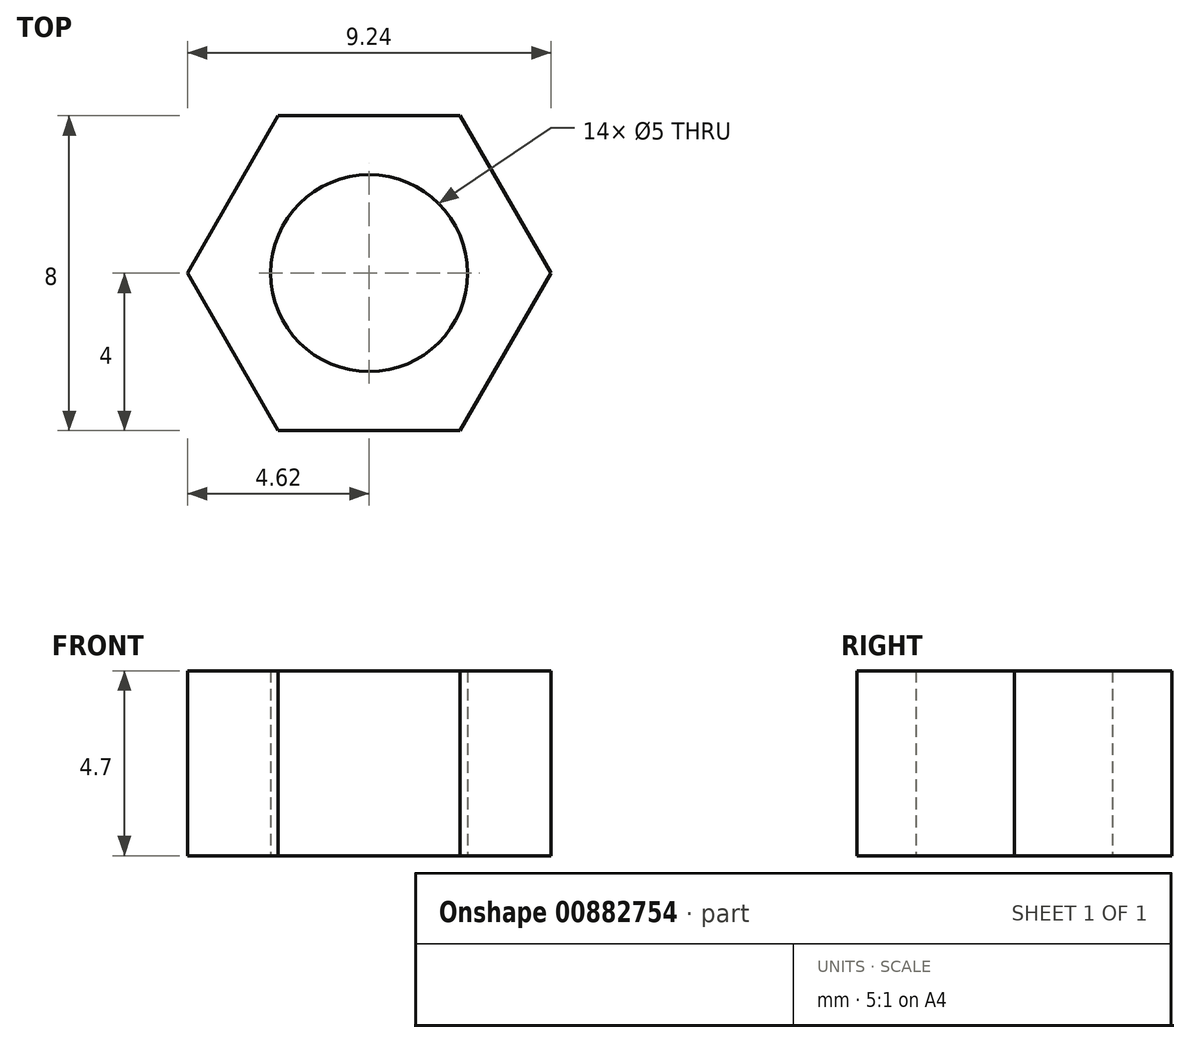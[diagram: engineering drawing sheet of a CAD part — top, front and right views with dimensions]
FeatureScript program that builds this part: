
annotation { "Feature Type Name" : "Feature", "Feature Type Description" : "" }
export const myFeature = defineFeature(function(context is Context, id is Id, definition is map)
    precondition{}
    {
        {
            var Q0;
            Q0=qCreatedBy(makeId("Top.planeOp"),FACE);
            var sketch = newSketch(context, id + "F0", { "sketchPlane" : qUnion([Q0])});
            skCircle(sketch, "E0", {"center": v(0, 0) * mm, "radius": 2.5 * mm});
            skCircle(sketch, "E1", {"center": v(0, 0) * mm, "radius": 4 * mm});
            skCircle(sketch, "E2.cCircle", {"center": v(0, 0) * mm, "radius": 4 * mm, "construction": true});
            skPoint(sketch, "E3", {"position": v(3.46, -2) * mm});
            skLineSegment(sketch, "E4", {"start": v(0, 0) * mm, "end": v(3.46, -2) * mm});
            skLineSegment(sketch, "E5.0", {"start": v(4.62, 0) * mm, "end": v(2.3, -4) * mm});
            skLineSegment(sketch, "E5.1", {"start": v(2.3, -4) * mm, "end": v(-2.3, -4) * mm});
            skLineSegment(sketch, "E5.2", {"start": v(-2.3, -4) * mm, "end": v(-4.62, 0) * mm});
            skLineSegment(sketch, "E5.3", {"start": v(-4.62, 0) * mm, "end": v(-2.3, 4) * mm});
            skLineSegment(sketch, "E5.4", {"start": v(-2.3, 4) * mm, "end": v(2.3, 4) * mm});
            skLineSegment(sketch, "E5.5", {"start": v(2.3, 4) * mm, "end": v(4.62, 0) * mm});
            skSolve(sketch);
        }
        {
            var Q0;
            Q0=qSketchRegion(id+"F0",true);
            extrude(context, id + "F1", {"entities" : qUnion([Q0]), "depth" : 4.7 * mm, "offsetDistance" : 25 * mm});
        }
    });
